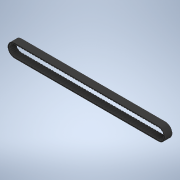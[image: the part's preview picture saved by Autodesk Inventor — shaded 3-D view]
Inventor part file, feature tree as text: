
AUTODESK INVENTOR PART (.ipt)
format: ipt  version: 2021 (Build 250183000, 183)  size: 988,672 bytes
history: native  units: in
note: dims shown in document units (in); Inventor stores cm internally (conversion verified against a paired STEP export)
features: other x120, sketch x3, pattern_linear x2, extrude x2, fillet x1
ambient origin geometry x8: Origin, YZ Plane, XZ Plane, XY Plane, X Axis, Y Axis, Z Axis, Center Point
bodies: Solid1 (feature_tree)
feature tree (128):
  sketch  "Sketch1"  dims[d0=0.6693in]
  other  "Work Point1"
  pattern_linear  "Rectangular Pattern1"  Count1=120 Spacing1=0.3937in
  extrude  "Extrusion1"  Depth=0.4134in
  fillet  "Fillet1"  Radius=0.0394in
  pattern_linear  "Rectangular Pattern2"  Spacing1=0.0394in  [1 undecoded]
  extrude  "Extrusion2"  Depth=0.4134in TaperAngle=0.0deg
  other  "Work Point2"
  other  "Work Point3"
  other  "Work Point4"
  other  "Work Point5"
  other  "Work Point6"
  other  "Work Point7"
  other  "Work Point8"
  other  "Work Point9"
  other  "Work Point10"
  other  "Work Point11"
  other  "Work Point12"
  other  "Work Point13"
  other  "Work Point14"
  other  "Work Point15"
  other  "Work Point16"
  other  "Work Point17"
  other  "Work Point18"
  other  "Work Point19"
  other  "Work Point20"
  other  "Work Point21"
  other  "Work Point22"
  other  "Work Point23"
  other  "Work Point24"
  other  "Work Point25"
  other  "Work Point26"
  other  "Work Point27"
  other  "Work Point28"
  other  "Work Point29"
  other  "Work Point30"
  other  "Work Point31"
  other  "Work Point32"
  other  "Work Point33"
  other  "Work Point34"
  other  "Work Point35"
  other  "Work Point36"
  other  "Work Point37"
  other  "Work Point38"
  other  "Work Point39"
  other  "Work Point40"
  other  "Work Point41"
  other  "Work Point42"
  other  "Work Point43"
  other  "Work Point44"
  other  "Work Point45"
  other  "Work Point46"
  other  "Work Point47"
  other  "Work Point48"
  other  "Work Point49"
  other  "Work Point50"
  other  "Work Point51"
  other  "Work Point52"
  other  "Work Point53"
  other  "Work Point54"
  other  "Work Point55"
  other  "Work Point56"
  other  "Work Point57"
  other  "Work Point58"
  other  "Work Point59"
  other  "Work Point60"
  other  "Work Point61"
  other  "Work Point62"
  other  "Work Point63"
  other  "Work Point64"
  other  "Work Point65"
  other  "Work Point66"
  other  "Work Point67"
  other  "Work Point68"
  other  "Work Point69"
  other  "Work Point70"
  other  "Work Point71"
  other  "Work Point72"
  other  "Work Point73"
  other  "Work Point74"
  other  "Work Point75"
  other  "Work Point76"
  other  "Work Point77"
  other  "Work Point78"
  other  "Work Point79"
  other  "Work Point80"
  other  "Work Point81"
  other  "Work Point82"
  other  "Work Point83"
  other  "Work Point84"
  other  "Work Point85"
  other  "Work Point86"
  other  "Work Point87"
  other  "Work Point88"
  other  "Work Point89"
  other  "Work Point90"
  other  "Work Point91"
  other  "Work Point92"
  other  "Work Point93"
  other  "Work Point94"
  other  "Work Point95"
  other  "Work Point96"
  other  "Work Point97"
  other  "Work Point98"
  other  "Work Point99"
  other  "Work Point100"
  other  "Work Point101"
  other  "Work Point102"
  other  "Work Point103"
  other  "Work Point104"
  other  "Work Point105"
  other  "Work Point106"
  other  "Work Point107"
  other  "Work Point108"
  other  "Work Point109"
  other  "Work Point110"
  other  "Work Point111"
  other  "Work Point112"
  other  "Work Point113"
  other  "Work Point114"
  other  "Work Point115"
  other  "Work Point116"
  other  "Work Point117"
  other  "Work Point118"
  other  "Work Point119"
  other  "Work Point120"
  sketch  "Sketch2"  dims[d1=8.4646in d2=47.2441in d4=0.3937in]
  sketch  "Sketch3"  dims[d5=0.1181in d6=0.0394in d7=0.0394in d8=0.0394in d9=0.4134in d10=0.0in d11=0.0197in d12=47.2441in d14=0.0591in d15=0.4134in d16=0.0in]
note: 1 required parameter value undecoded (feature->parameter linkage not recoverable at this tier; creation-order binding heuristic only, values carry confidence <= 0.55)
